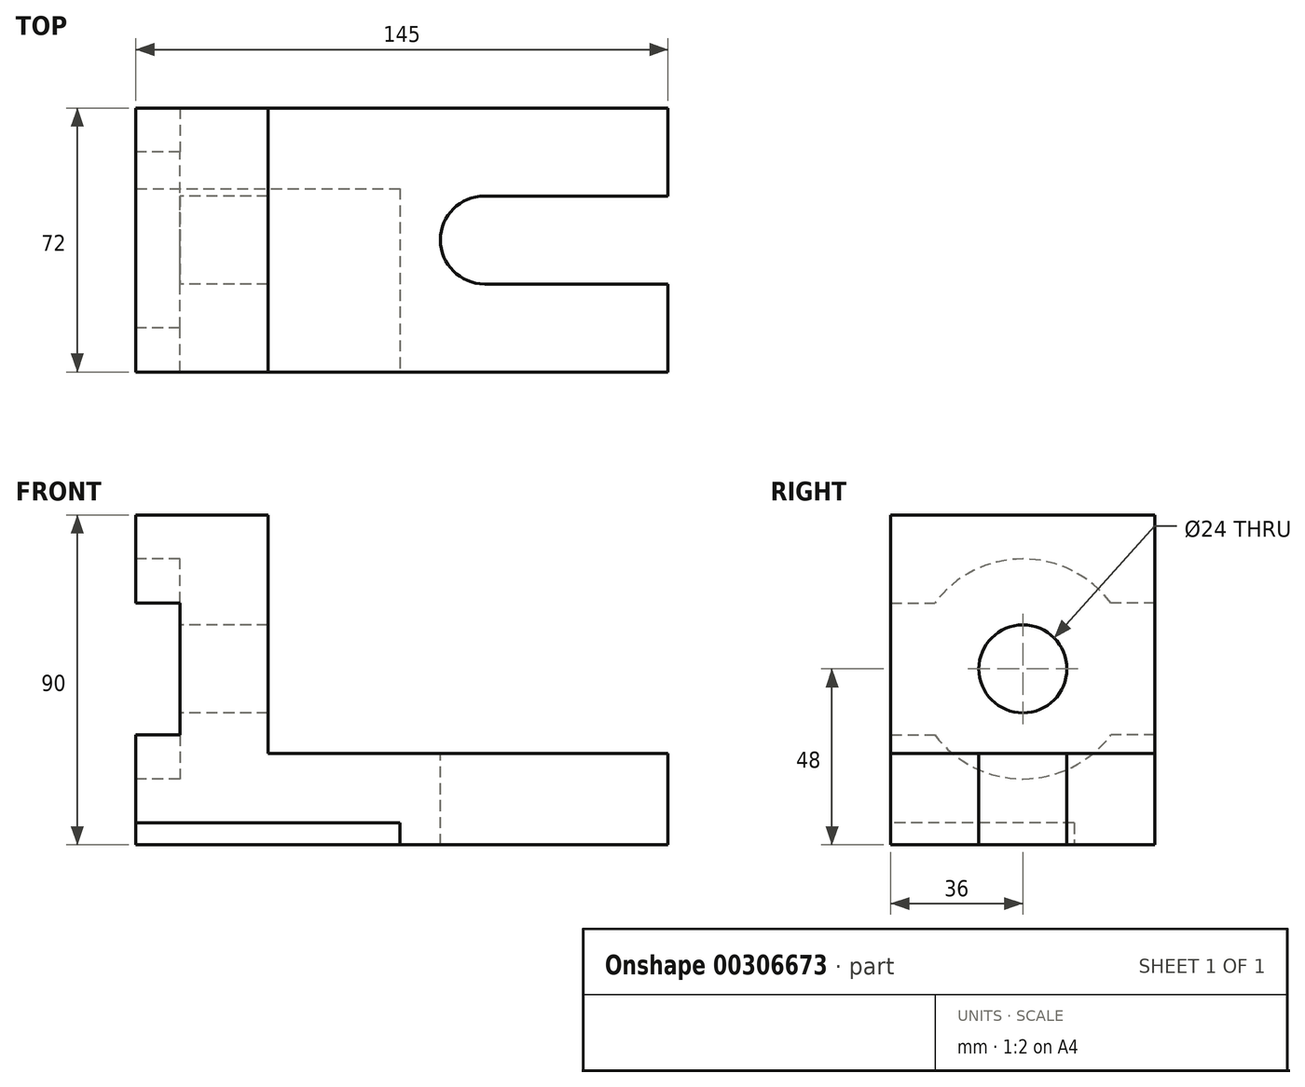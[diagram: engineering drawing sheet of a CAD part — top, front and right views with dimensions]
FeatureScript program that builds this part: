
annotation { "Feature Type Name" : "Feature", "Feature Type Description" : "" }
export const myFeature = defineFeature(function(context is Context, id is Id, definition is map)
    precondition{}
    {
        {
            var Q0;
            Q0=qCreatedBy(makeId("Front.planeOp"),FACE);
            var sketch = newSketch(context, id + "F0", { "sketchPlane" : qUnion([Q0])});
            skLineSegment(sketch, "E0", {"start": v(0, 0) * mm, "end": v(73, 0) * mm});
            skLineSegment(sketch, "E1", {"start": v(73, 0) * mm, "end": v(73, 25) * mm});
            skLineSegment(sketch, "E2", {"start": v(73, 25) * mm, "end": v(-36, 25) * mm});
            skLineSegment(sketch, "E3", {"start": v(-36, 25) * mm, "end": v(-36, 90) * mm});
            skLineSegment(sketch, "E4", {"start": v(-36, 90) * mm, "end": v(-72, 90) * mm});
            skLineSegment(sketch, "E5", {"start": v(-72, 90) * mm, "end": v(-72, 0) * mm});
            skLineSegment(sketch, "E6", {"start": v(-72, 0) * mm, "end": v(0, 0) * mm});
            skPoint(sketch, "E7", {"position": v(73, 0) * mm});
            skLineSegment(sketch, "E8", {"start": v(73, 0) * mm, "end": v(23, 0) * mm, "construction": true});
            skPoint(sketch, "E9", {"position": v(23, 0) * mm});
            skPoint(sketch, "E10", {"position": v(-72, 0) * mm});
            skSolve(sketch);
        }
        {
            var Q0;
            Q0=makeQuery(id+"F0.imprint","IMPRINT",FACE,{"disambiguationData":[TD([[makeQuery(id+"F0.imprint","IMPRINT",EDGE,{"derivedFrom":sQuery(id+"F0.wireOp",EDGE,"E0")}),1.0]])]});
            extrude(context, id + "F1", {"entities" : qUnion([Q0]), "endBound" : BoundingType.SYMMETRIC, "depth" : 72 * mm});
        }
        {
            var Q0;
            Q0=makeQuery(id+"F1.opExtrude","SWEPT_FACE",FACE,{"disambiguationData":[OSD([sQuery(id+"F0.wireOp",EDGE,"E2")])]});
            var sketch = newSketch(context, id + "F2", { "sketchPlane" : qUnion([Q0])});
            skPoint(sketch, "E11.0", {"position": v(23, 0) * mm});
            skArc(sketch, "E12", {"start": v(23, 12) * mm, "mid": v(11, 0) * mm, "end": v(23, -12) * mm});
            skLineSegment(sketch, "E13", {"start": v(23, 12) * mm, "end": v(73, 12) * mm});
            skLineSegment(sketch, "E14", {"start": v(23, -12) * mm, "end": v(73, -12) * mm});
            skLineSegment(sketch, "E15", {"start": v(73, -12) * mm, "end": v(73, 12) * mm});
            skSolve(sketch);
        }
        {
            var Q0;
            Q0 = qSketchRegion(id + "F2", true);
            var Q1;
            Q1=makeQuery(id+"F2.imprint","IMPRINT",FACE,{"disambiguationData":[TD([[makeQuery(id+"F2.imprint","IMPRINT",EDGE,{"derivedFrom":sQuery(id+"F2.wireOp",EDGE,"E12")}),1.0]])]});
            extrude(context, id + "F3", {"entities" : qUnion([Q0, Q1]), "operationType" : NewBodyOperationType.REMOVE, "endBound" : BoundingType.THROUGH_ALL, "oppositeDirection" : true, "depth" : 25 * mm});
        }
        {
            var Q0;
            Q0=makeQuery(id+"F1.opExtrude","CAP_FACE",FACE,{"disambiguationData":[OSD([sQuery(id+"F0.wireOp",EDGE,"E0"),sQuery(id+"F0.wireOp",EDGE,"E1"),sQuery(id+"F0.wireOp",EDGE,"E2"),sQuery(id+"F0.wireOp",EDGE,"E3"),sQuery(id+"F0.wireOp",EDGE,"E4"),sQuery(id+"F0.wireOp",EDGE,"E5"),sQuery(id+"F0.wireOp",EDGE,"E6")])],"isStart":false});
            var sketch = newSketch(context, id + "F4", { "sketchPlane" : qUnion([Q0])});
            skLineSegment(sketch, "E16", {"start": v(-72, 0) * mm, "end": v(-72, 6) * mm});
            skLineSegment(sketch, "E17", {"start": v(-72, 6) * mm, "end": v(0, 6) * mm});
            skLineSegment(sketch, "E18", {"start": v(0, 6) * mm, "end": v(0, 0) * mm});
            skLineSegment(sketch, "E19", {"start": v(0, 0) * mm, "end": v(-72, 0) * mm});
            skSolve(sketch);
        }
        {
            var Q0;
            Q0=makeQuery(id+"F4.imprint","IMPRINT",FACE,{"disambiguationData":[TD([[makeQuery(id+"F4.imprint","IMPRINT",EDGE,{"derivedFrom":sQuery(id+"F4.wireOp",EDGE,"E16")}),1.0]])]});
            extrude(context, id + "F5", {"entities" : qUnion([Q0]), "operationType" : NewBodyOperationType.REMOVE, "oppositeDirection" : true, "depth" : 50 * mm});
        }
        {
            var Q0;
            Q0=makeQuery(id+"F1.opExtrude","SWEPT_FACE",FACE,{"disambiguationData":[OSD([sQuery(id+"F0.wireOp",EDGE,"E5")])]});
            var sketch = newSketch(context, id + "F6", { "sketchPlane" : qUnion([Q0])});
            skPoint(sketch, "E20.0", {"position": v(0, 0) * mm});
            skLineSegment(sketch, "E21", {"start": v(0, 0) * mm, "end": v(0, 48) * mm, "construction": true});
            skArc(sketch, "E22", {"start": v(-24, 30) * mm, "mid": v(0, 18) * mm, "end": v(24, 30) * mm});
            skCircle(sketch, "E23", {"center": v(0, 48) * mm, "radius": 12 * mm});
            skLineSegment(sketch, "E24", {"start": v(-36, 0) * mm, "end": v(-36, 30) * mm, "construction": true});
            skLineSegment(sketch, "E25", {"start": v(-36, 90) * mm, "end": v(-36, 66) * mm, "construction": true});
            skLineSegment(sketch, "E26", {"start": v(36, 90) * mm, "end": v(36, 66) * mm, "construction": true});
            skLineSegment(sketch, "E27", {"start": v(36, 0) * mm, "end": v(36, 30) * mm, "construction": true});
            skLineSegment(sketch, "E28", {"start": v(36, 30) * mm, "end": v(24, 30) * mm});
            skLineSegment(sketch, "E29", {"start": v(-36, 30) * mm, "end": v(-24, 30) * mm});
            skLineSegment(sketch, "E30", {"start": v(36, 66) * mm, "end": v(24, 66) * mm});
            skLineSegment(sketch, "E31", {"start": v(-36, 66) * mm, "end": v(-24, 66) * mm});
            skLineSegment(sketch, "E32", {"start": v(-36, 66) * mm, "end": v(-36, 30) * mm});
            skLineSegment(sketch, "E33", {"start": v(36, 66) * mm, "end": v(36, 30) * mm});
            skArc(sketch, "E34.trimOffspring", {"start": v(24, 66) * mm, "mid": v(0, 78) * mm, "end": v(-24, 66) * mm});
            skSolve(sketch);
        }
        {
            var Q0;
            Q0 = qSketchRegion(id + "F6", true);
            extrude(context, id + "F7", {"entities" : qUnion([Q0]), "operationType" : NewBodyOperationType.REMOVE, "oppositeDirection" : true, "depth" : 12 * mm});
        }
        {
            var Q0;
            Q0=makeQuery(id+"F7.boolean.opBoolean","SPLIT",FACE,{"disambiguationData":[TD([makeQuery(id+"F7.opExtrude","SWEPT_FACE",FACE,{"disambiguationData":[OSD([sQuery(id+"F6.wireOp",EDGE,"E23")])]})])],"derivedFrom":makeQuery(id+"F1.opExtrude","SWEPT_FACE",FACE,{"disambiguationData":[OSD([sQuery(id+"F0.wireOp",EDGE,"E5")])]})});
            extrude(context, id + "F8", {"entities" : qUnion([Q0]), "operationType" : NewBodyOperationType.REMOVE, "endBound" : BoundingType.THROUGH_ALL, "oppositeDirection" : true, "depth" : 25 * mm});
        }
    });
